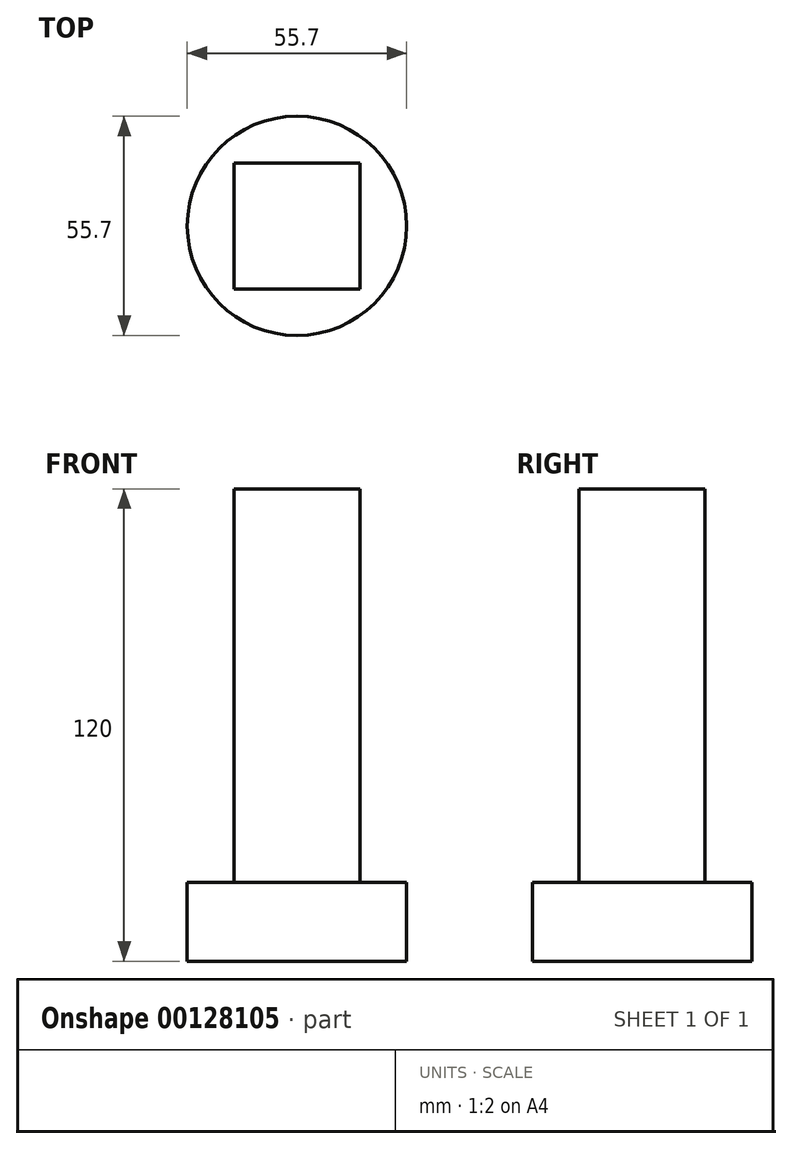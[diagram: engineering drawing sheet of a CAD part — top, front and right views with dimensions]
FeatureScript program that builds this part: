
annotation { "Feature Type Name" : "Feature", "Feature Type Description" : "" }
export const myFeature = defineFeature(function(context is Context, id is Id, definition is map)
    precondition{}
    {
        {
            var Q0;
            Q0=qCreatedBy(makeId("Top.planeOp"),FACE);
            var sketch = newSketch(context, id + "F0", { "sketchPlane" : qUnion([Q0])});
            skCircle(sketch, "E0", {"center": v(0, 0) * mm, "radius": 27.85 * mm});
            skSolve(sketch);
        }
        {
            var Q0;
            Q0 = qSketchRegion(id + "F0", true);
            extrude(context, id + "F1", {"entities" : qUnion([Q0]), "depth" : 20 * mm});
        }
        {
            var Q0;
            Q0=makeQuery(id+"F1.opExtrude","CAP_FACE",FACE,{"disambiguationData":[OSD([sQuery(id+"F0.wireOp",EDGE,"E0")])],"isStart":false});
            var sketch = newSketch(context, id + "F2", { "sketchPlane" : qUnion([Q0])});
            skLineSegment(sketch, "E1.bottom", {"start": v(16, 16) * mm, "end": v(-16, 16) * mm});
            skLineSegment(sketch, "E1.top", {"start": v(16, -16) * mm, "end": v(-16, -16) * mm});
            skLineSegment(sketch, "E1.left", {"start": v(16, 16) * mm, "end": v(16, -16) * mm});
            skLineSegment(sketch, "E1.right", {"start": v(-16, 16) * mm, "end": v(-16, -16) * mm});
            skPoint(sketch, "E1.middle", {"position": v(0, 0) * mm});
            skSolve(sketch);
        }
        {
            var Q0;
            Q0 = qSketchRegion(id + "F2", true);
            extrude(context, id + "F3", {"entities" : qUnion([Q0]), "operationType" : NewBodyOperationType.ADD, "depth" : 100 * mm});
        }
    });
